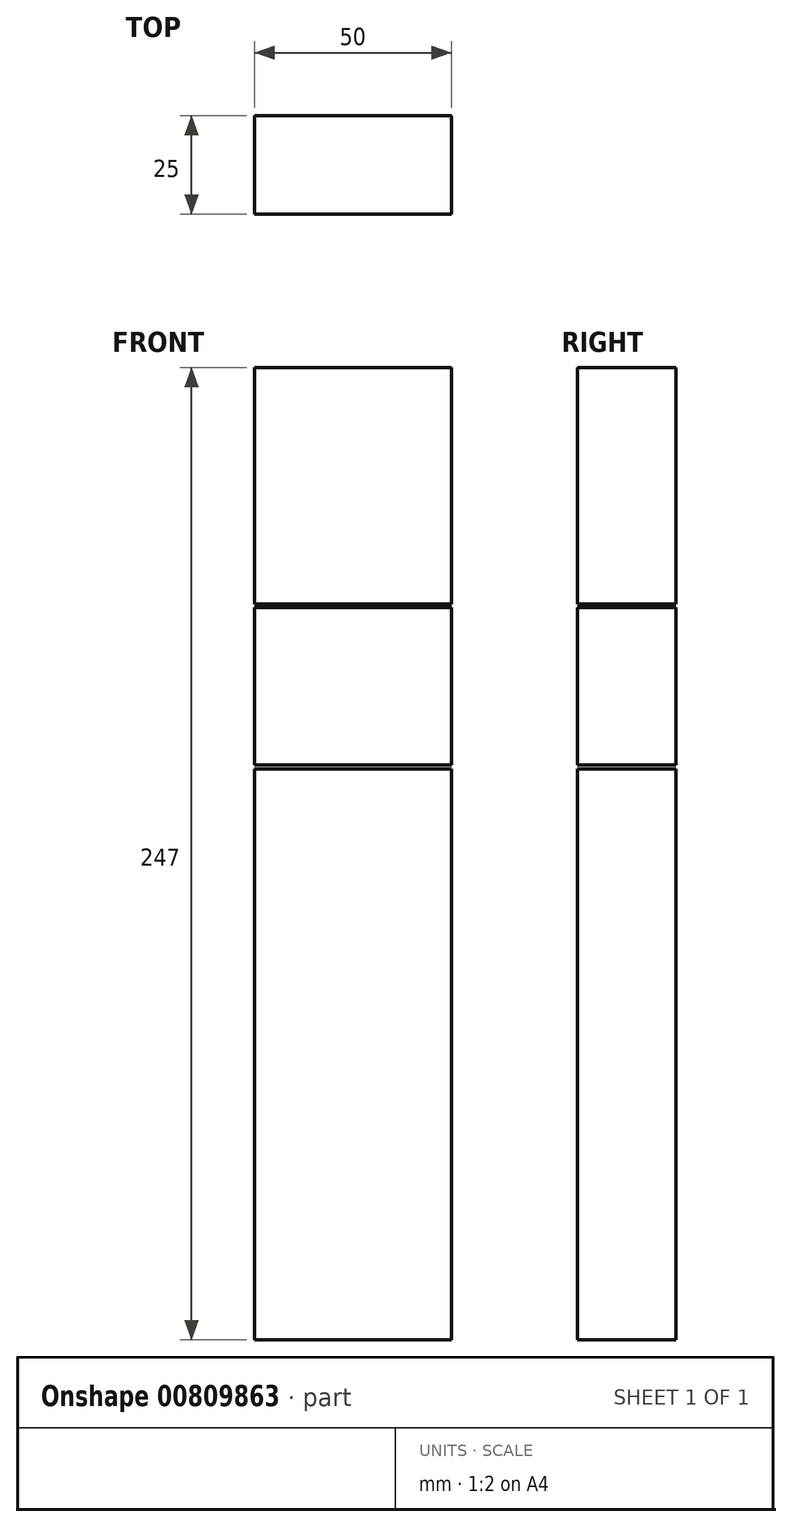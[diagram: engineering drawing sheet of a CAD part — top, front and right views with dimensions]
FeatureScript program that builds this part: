
annotation { "Feature Type Name" : "Feature", "Feature Type Description" : "" }
export const myFeature = defineFeature(function(context is Context, id is Id, definition is map)
    precondition{}
    {
        {
            var Q0;
            Q0=qCreatedBy(makeId("Front.planeOp"),FACE);
            var sketch = newSketch(context, id + "F0", { "sketchPlane" : qUnion([Q0])});
            skLineSegment(sketch, "E0.bottom", {"start": v(0, 0) * mm, "end": v(50, 0) * mm});
            skLineSegment(sketch, "E0.top", {"start": v(0, 145) * mm, "end": v(50, 145) * mm});
            skLineSegment(sketch, "E0.left", {"start": v(0, 0) * mm, "end": v(0, 145) * mm});
            skLineSegment(sketch, "E0.right", {"start": v(50, 0) * mm, "end": v(50, 145) * mm});
            skLineSegment(sketch, "E1.bottom", {"start": v(0, 146) * mm, "end": v(50, 146) * mm});
            skLineSegment(sketch, "E1.top", {"start": v(0, 186) * mm, "end": v(50, 186) * mm});
            skLineSegment(sketch, "E1.left", {"start": v(0, 146) * mm, "end": v(0, 186) * mm});
            skLineSegment(sketch, "E1.right", {"start": v(50, 146) * mm, "end": v(50, 186) * mm});
            skLineSegment(sketch, "E2.bottom", {"start": v(0, 187) * mm, "end": v(50, 187) * mm});
            skLineSegment(sketch, "E2.top", {"start": v(0, 247) * mm, "end": v(50, 247) * mm});
            skLineSegment(sketch, "E2.left", {"start": v(0, 187) * mm, "end": v(0, 247) * mm});
            skLineSegment(sketch, "E2.right", {"start": v(50, 187) * mm, "end": v(50, 247) * mm});
            skSolve(sketch);
        }
        {
            var Q0;
            Q0=qSketchRegion(id+"F0",true);
            extrude(context, id + "F1", {"entities" : qUnion([Q0]), "oppositeDirection" : true, "depth" : 25 * mm, "offsetDistance" : 25 * mm});
        }
    });
